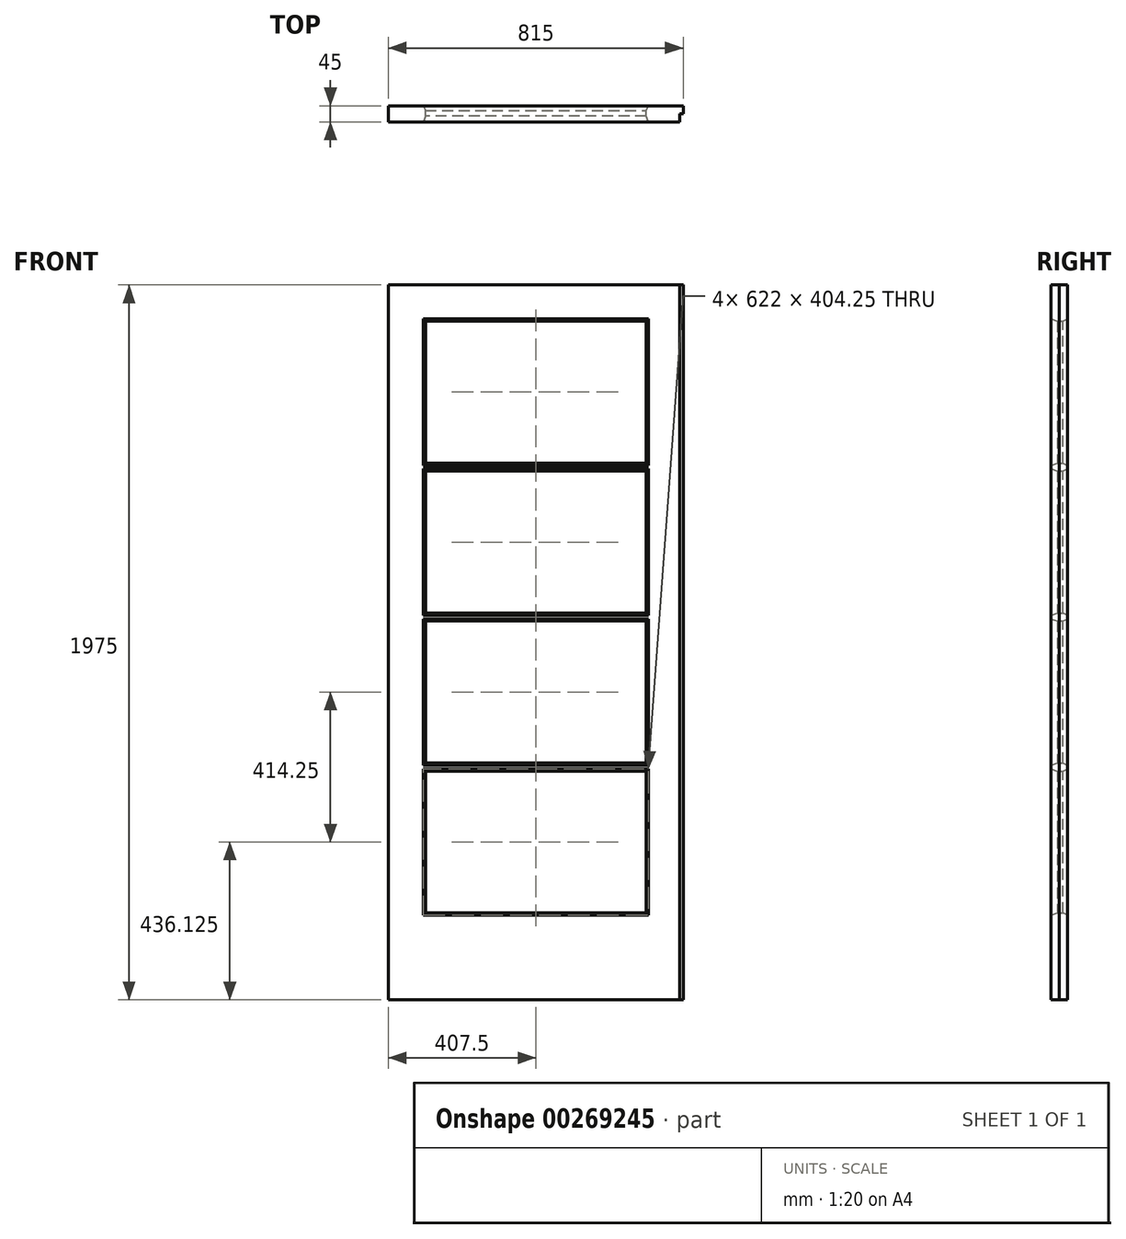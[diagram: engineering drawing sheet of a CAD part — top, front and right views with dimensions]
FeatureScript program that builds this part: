
annotation { "Feature Type Name" : "Feature", "Feature Type Description" : "" }
export const myFeature = defineFeature(function(context is Context, id is Id, definition is map)
    precondition{}
    {
        {
            var Q0;
            Q0=qCreatedBy(makeId("Front.planeOp"),FACE);
            var sketch = newSketch(context, id + "F0", { "sketchPlane" : qUnion([Q0])});
            skLineSegment(sketch, "E0.bottom", {"start": v(-407.5, 987.5) * mm, "end": v(407.5, 987.5) * mm});
            skLineSegment(sketch, "E0.top", {"start": v(-407.5, -987.5) * mm, "end": v(407.5, -987.5) * mm});
            skLineSegment(sketch, "E0.left", {"start": v(-407.5, 987.5) * mm, "end": v(-407.5, -987.5) * mm});
            skLineSegment(sketch, "E0.right", {"start": v(407.5, 987.5) * mm, "end": v(407.5, -987.5) * mm});
            skPoint(sketch, "E0.middle", {"position": v(0, 0) * mm});
            skLineSegment(sketch, "E1.bottom", {"start": v(-305, 887.5) * mm, "end": v(305, 887.5) * mm});
            skLineSegment(sketch, "E1.top", {"start": v(-305, 495.25) * mm, "end": v(305, 495.25) * mm});
            skLineSegment(sketch, "E1.left", {"start": v(-305, 887.5) * mm, "end": v(-305, 495.25) * mm});
            skLineSegment(sketch, "E1.right", {"start": v(305, 887.5) * mm, "end": v(305, 495.25) * mm});
            skLineSegment(sketch, "E2.bottom", {"start": v(-305, 473.25) * mm, "end": v(305, 473.25) * mm});
            skLineSegment(sketch, "E2.top", {"start": v(-305, 81) * mm, "end": v(305, 81) * mm});
            skLineSegment(sketch, "E2.left", {"start": v(-305, 473.25) * mm, "end": v(-305, 81) * mm});
            skLineSegment(sketch, "E2.right", {"start": v(305, 473.25) * mm, "end": v(305, 81) * mm});
            skLineSegment(sketch, "E3.bottom", {"start": v(-305, 59) * mm, "end": v(305, 59) * mm});
            skLineSegment(sketch, "E3.top", {"start": v(-305, -333.25) * mm, "end": v(305, -333.25) * mm});
            skLineSegment(sketch, "E3.left", {"start": v(-305, 59) * mm, "end": v(-305, -333.25) * mm});
            skLineSegment(sketch, "E3.right", {"start": v(305, 59) * mm, "end": v(305, -333.25) * mm});
            skLineSegment(sketch, "E4.bottom", {"start": v(-305, -355.25) * mm, "end": v(305, -355.25) * mm});
            skLineSegment(sketch, "E4.top", {"start": v(-305, -747.5) * mm, "end": v(305, -747.5) * mm});
            skLineSegment(sketch, "E4.left", {"start": v(-305, -355.25) * mm, "end": v(-305, -747.5) * mm});
            skLineSegment(sketch, "E4.right", {"start": v(305, -355.25) * mm, "end": v(305, -747.5) * mm});
            skLineSegment(sketch, "E5", {"start": v(-305, 495.25) * mm, "end": v(-305, 473.25) * mm, "construction": true});
            skLineSegment(sketch, "E6", {"start": v(-305, 81) * mm, "end": v(-305, 59) * mm, "construction": true});
            skLineSegment(sketch, "E7", {"start": v(-305, -333.25) * mm, "end": v(-305, -355.25) * mm, "construction": true});
            skSolve(sketch);
        }
        {
            var Q0;
            Q0=makeQuery(id+"F0.imprint","IMPRINT",FACE,{"disambiguationData":[TD([[makeQuery(id+"F0.imprint","IMPRINT",EDGE,{"derivedFrom":sQuery(id+"F0.wireOp",EDGE,"E0.bottom")}),-1.0]])]});
            extrude(context, id + "F1", {"entities" : qUnion([Q0]), "endBound" : BoundingType.SYMMETRIC, "depth" : 45 * mm});
        }
        {
            var Q0;
            Q0=makeQuery(id+"F1.opExtrude","CAP_EDGE",EDGE,{"disambiguationData":[OSD([sQuery(id+"F0.wireOp",EDGE,"E4.right")])],"isStart":false});
            var Q1;
            Q1=makeQuery(id+"F1.opExtrude","CAP_EDGE",EDGE,{"disambiguationData":[OSD([sQuery(id+"F0.wireOp",EDGE,"E4.bottom")])],"isStart":false});
            var Q2;
            Q2=makeQuery(id+"F1.opExtrude","CAP_EDGE",EDGE,{"disambiguationData":[OSD([sQuery(id+"F0.wireOp",EDGE,"E3.right")])],"isStart":false});
            var Q3;
            Q3=makeQuery(id+"F1.opExtrude","CAP_EDGE",EDGE,{"disambiguationData":[OSD([sQuery(id+"F0.wireOp",EDGE,"E3.bottom")])],"isStart":false});
            var Q4;
            Q4=makeQuery(id+"F1.opExtrude","CAP_EDGE",EDGE,{"disambiguationData":[OSD([sQuery(id+"F0.wireOp",EDGE,"E2.right")])],"isStart":false});
            var Q5;
            Q5=makeQuery(id+"F1.opExtrude","CAP_EDGE",EDGE,{"disambiguationData":[OSD([sQuery(id+"F0.wireOp",EDGE,"E2.bottom")])],"isStart":false});
            var Q6;
            Q6=makeQuery(id+"F1.opExtrude","CAP_EDGE",EDGE,{"disambiguationData":[OSD([sQuery(id+"F0.wireOp",EDGE,"E1.right")])],"isStart":false});
            var Q7;
            Q7=makeQuery(id+"F1.opExtrude","CAP_EDGE",EDGE,{"disambiguationData":[OSD([sQuery(id+"F0.wireOp",EDGE,"E1.bottom")])],"isStart":false});
            var Q8;
            Q8=makeQuery(id+"F1.opExtrude","CAP_EDGE",EDGE,{"disambiguationData":[OSD([sQuery(id+"F0.wireOp",EDGE,"E1.left")])],"isStart":false});
            var Q9;
            Q9=makeQuery(id+"F1.opExtrude","CAP_EDGE",EDGE,{"disambiguationData":[OSD([sQuery(id+"F0.wireOp",EDGE,"E1.top")])],"isStart":false});
            var Q10;
            Q10=makeQuery(id+"F1.opExtrude","CAP_EDGE",EDGE,{"disambiguationData":[OSD([sQuery(id+"F0.wireOp",EDGE,"E2.left")])],"isStart":false});
            var Q11;
            Q11=makeQuery(id+"F1.opExtrude","CAP_EDGE",EDGE,{"disambiguationData":[OSD([sQuery(id+"F0.wireOp",EDGE,"E2.top")])],"isStart":false});
            var Q12;
            Q12=makeQuery(id+"F1.opExtrude","CAP_EDGE",EDGE,{"disambiguationData":[OSD([sQuery(id+"F0.wireOp",EDGE,"E3.left")])],"isStart":false});
            var Q13;
            Q13=makeQuery(id+"F1.opExtrude","CAP_EDGE",EDGE,{"disambiguationData":[OSD([sQuery(id+"F0.wireOp",EDGE,"E3.top")])],"isStart":false});
            var Q14;
            Q14=makeQuery(id+"F1.opExtrude","CAP_EDGE",EDGE,{"disambiguationData":[OSD([sQuery(id+"F0.wireOp",EDGE,"E4.left")])],"isStart":false});
            var Q15;
            Q15=makeQuery(id+"F1.opExtrude","CAP_EDGE",EDGE,{"disambiguationData":[OSD([sQuery(id+"F0.wireOp",EDGE,"E4.top")])],"isStart":false});
            chamfer(context, id + "F2", {"entities" : qUnion([Q0, Q1, Q2, Q3, Q4, Q5, Q6, Q7, Q8, Q9, Q10, Q11, Q12, Q13, Q14, Q15]), "chamferType" : ChamferType.TWO_OFFSETS, "width1" : 6 * mm, "oppositeDirection" : false, "width2" : 17 * mm, "tangentPropagation" : true});
        }
        {
            var Q0;
            Q0=makeQuery(id+"F1.opExtrude","CAP_EDGE",EDGE,{"disambiguationData":[OSD([sQuery(id+"F0.wireOp",EDGE,"E4.top")])],"isStart":true});
            var Q1;
            Q1=makeQuery(id+"F1.opExtrude","CAP_EDGE",EDGE,{"disambiguationData":[OSD([sQuery(id+"F0.wireOp",EDGE,"E4.right")])],"isStart":true});
            var Q2;
            Q2=makeQuery(id+"F1.opExtrude","CAP_EDGE",EDGE,{"disambiguationData":[OSD([sQuery(id+"F0.wireOp",EDGE,"E4.bottom")])],"isStart":true});
            var Q3;
            Q3=makeQuery(id+"F1.opExtrude","CAP_EDGE",EDGE,{"disambiguationData":[OSD([sQuery(id+"F0.wireOp",EDGE,"E4.left")])],"isStart":true});
            var Q4;
            Q4=makeQuery(id+"F1.opExtrude","CAP_EDGE",EDGE,{"disambiguationData":[OSD([sQuery(id+"F0.wireOp",EDGE,"E3.left")])],"isStart":true});
            var Q5;
            Q5=makeQuery(id+"F1.opExtrude","CAP_EDGE",EDGE,{"disambiguationData":[OSD([sQuery(id+"F0.wireOp",EDGE,"E3.bottom")])],"isStart":true});
            var Q6;
            Q6=makeQuery(id+"F1.opExtrude","CAP_EDGE",EDGE,{"disambiguationData":[OSD([sQuery(id+"F0.wireOp",EDGE,"E2.left")])],"isStart":true});
            var Q7;
            Q7=makeQuery(id+"F1.opExtrude","CAP_EDGE",EDGE,{"disambiguationData":[OSD([sQuery(id+"F0.wireOp",EDGE,"E3.top")])],"isStart":true});
            var Q8;
            Q8=makeQuery(id+"F1.opExtrude","CAP_EDGE",EDGE,{"disambiguationData":[OSD([sQuery(id+"F0.wireOp",EDGE,"E3.right")])],"isStart":true});
            var Q9;
            Q9=makeQuery(id+"F1.opExtrude","CAP_EDGE",EDGE,{"disambiguationData":[OSD([sQuery(id+"F0.wireOp",EDGE,"E2.top")])],"isStart":true});
            var Q10;
            Q10=makeQuery(id+"F1.opExtrude","CAP_EDGE",EDGE,{"disambiguationData":[OSD([sQuery(id+"F0.wireOp",EDGE,"E2.right")])],"isStart":true});
            var Q11;
            Q11=makeQuery(id+"F1.opExtrude","CAP_EDGE",EDGE,{"disambiguationData":[OSD([sQuery(id+"F0.wireOp",EDGE,"E2.bottom")])],"isStart":true});
            var Q12;
            Q12=makeQuery(id+"F1.opExtrude","CAP_EDGE",EDGE,{"disambiguationData":[OSD([sQuery(id+"F0.wireOp",EDGE,"E1.right")])],"isStart":true});
            var Q13;
            Q13=makeQuery(id+"F1.opExtrude","CAP_EDGE",EDGE,{"disambiguationData":[OSD([sQuery(id+"F0.wireOp",EDGE,"E1.bottom")])],"isStart":true});
            var Q14;
            Q14=makeQuery(id+"F1.opExtrude","CAP_EDGE",EDGE,{"disambiguationData":[OSD([sQuery(id+"F0.wireOp",EDGE,"E1.left")])],"isStart":true});
            var Q15;
            Q15=makeQuery(id+"F1.opExtrude","CAP_EDGE",EDGE,{"disambiguationData":[OSD([sQuery(id+"F0.wireOp",EDGE,"E1.top")])],"isStart":true});
            chamfer(context, id + "F3", {"entities" : qUnion([Q0, Q1, Q2, Q3, Q4, Q5, Q6, Q7, Q8, Q9, Q10, Q11, Q12, Q13, Q14, Q15]), "chamferType" : ChamferType.TWO_OFFSETS, "width1" : 6 * mm, "oppositeDirection" : false, "width2" : 13 * mm, "tangentPropagation" : true});
        }
        {
            var Q0;
            Q0=makeQuery(id+"F1.opExtrude","SWEPT_FACE",FACE,{"disambiguationData":[OSD([sQuery(id+"F0.wireOp",EDGE,"E0.top")])]});
            var sketch = newSketch(context, id + "F4", { "sketchPlane" : qUnion([Q0])});
            skLineSegment(sketch, "E8.bottom", {"start": v(407.5, 22.5) * mm, "end": v(397.5, 22.5) * mm});
            skLineSegment(sketch, "E8.top", {"start": v(407.5, -0.5) * mm, "end": v(397.5, -0.5) * mm});
            skLineSegment(sketch, "E8.left", {"start": v(407.5, 22.5) * mm, "end": v(407.5, -0.5) * mm});
            skLineSegment(sketch, "E8.right", {"start": v(397.5, 22.5) * mm, "end": v(397.5, -0.5) * mm});
            skSolve(sketch);
        }
        {
            var Q0;
            Q0 = qSketchRegion(id + "F4", true);
            extrude(context, id + "F5", {"entities" : qUnion([Q0]), "operationType" : NewBodyOperationType.REMOVE, "endBound" : BoundingType.THROUGH_ALL, "oppositeDirection" : true, "depth" : 25 * mm});
        }
    });
